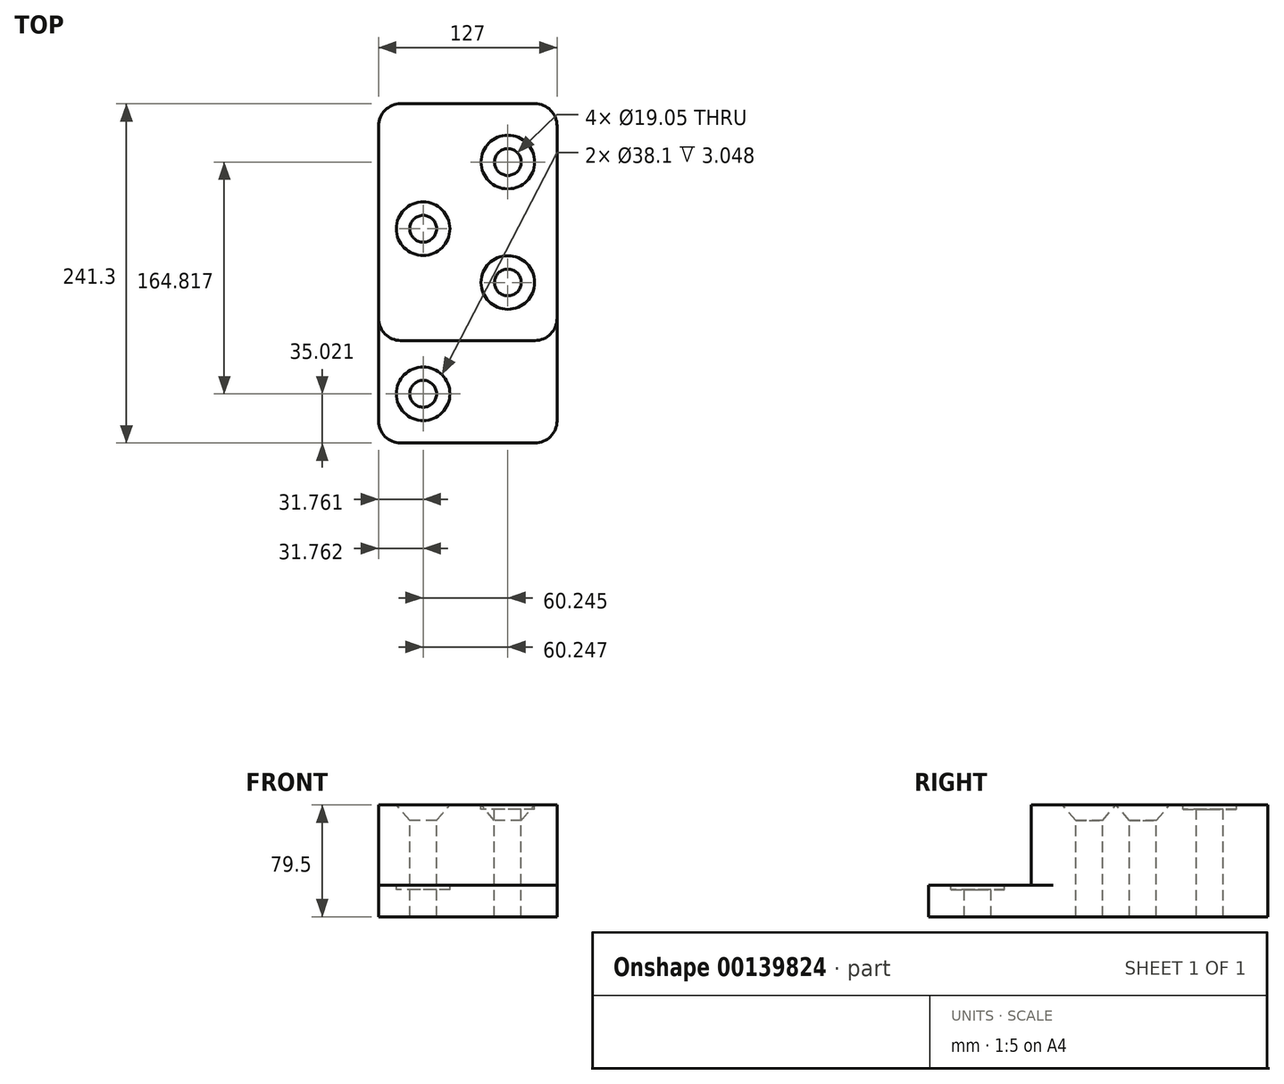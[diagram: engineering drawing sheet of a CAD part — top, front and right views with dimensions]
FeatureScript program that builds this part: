
annotation { "Feature Type Name" : "Feature", "Feature Type Description" : "" }
export const myFeature = defineFeature(function(context is Context, id is Id, definition is map)
    precondition{}
    {
        {
            var Q0;
            Q0=qCreatedBy(makeId("Top.planeOp"),FACE);
            var sketch = newSketch(context, id + "F0", { "sketchPlane" : qUnion([Q0])});
            skLineSegment(sketch, "E0", {"start": v(-63.5, 0) * mm, "end": v(63.5, 0) * mm});
            skLineSegment(sketch, "E1", {"start": v(-63.5, 0) * mm, "end": v(-63.5, -72.9) * mm});
            skLineSegment(sketch, "E2", {"start": v(-63.5, -72.9) * mm, "end": v(63.5, -72.9) * mm});
            skLineSegment(sketch, "E3", {"start": v(63.5, -72.9) * mm, "end": v(63.5, 0) * mm});
            skLineSegment(sketch, "E4", {"start": v(-63.5, 0) * mm, "end": v(-63.5, 168.4) * mm});
            skLineSegment(sketch, "E5", {"start": v(-63.5, 168.4) * mm, "end": v(63.5, 168.4) * mm});
            skLineSegment(sketch, "E6", {"start": v(63.5, 168.4) * mm, "end": v(63.5, 0) * mm});
            skSolve(sketch);
        }
        {
            var Q0;
            Q0=makeQuery(id+"F0.imprint","IMPRINT",FACE,{"disambiguationData":[TD([[makeQuery(id+"F0.imprint","IMPRINT",EDGE,{"derivedFrom":sQuery(id+"F0.wireOp",EDGE,"E0")}),1.0]])]});
            extrude(context, id + "F1", {"entities" : qUnion([Q0]), "depth" : 79.5 * mm});
        }
        {
            var Q0;
            Q0=makeQuery(id+"F0.imprint","IMPRINT",FACE,{"disambiguationData":[TD([[makeQuery(id+"F0.imprint","IMPRINT",EDGE,{"derivedFrom":sQuery(id+"F0.wireOp",EDGE,"E0")}),-1.0]])]});
            extrude(context, id + "F2", {"entities" : qUnion([Q0]), "operationType" : NewBodyOperationType.ADD, "depth" : 22.35 * mm});
        }
        {
            var Q0;
            Q0=makeQuery(id+"F1.opExtrude","CAP_FACE",FACE,{"disambiguationData":[OSD([sQuery(id+"F0.wireOp",EDGE,"E0"),sQuery(id+"F0.wireOp",EDGE,"E4"),sQuery(id+"F0.wireOp",EDGE,"E5"),sQuery(id+"F0.wireOp",EDGE,"E6")])],"isStart":false});
            var sketch = newSketch(context, id + "F3", { "sketchPlane" : qUnion([Q0])});
            skPoint(sketch, "E7", {"position": v(28.5, 126.94) * mm});
            skPoint(sketch, "E8", {"position": v(-31.74, 79.5) * mm});
            skPoint(sketch, "E9", {"position": v(28.48, 41.29) * mm});
            skPoint(sketch, "E10", {"position": v(-31.74, -37.88) * mm});
            skSolve(sketch);
        }
        {
            var Q0;
            Q0=sQuery(id+"F3.wireOp",VERTEX,"E7");
            var Q1;
            Q1=sQuery(id+"F3.wireOp",VERTEX,"E10");
            var Q2;
            Q2=makeQuery(id+"F1.opExtrude","SWEPT_BODY",BODY,{"disambiguationData":[OSD([sQuery(id+"F0.wireOp",EDGE,"E0"),sQuery(id+"F0.wireOp",EDGE,"E4"),sQuery(id+"F0.wireOp",EDGE,"E5"),sQuery(id+"F0.wireOp",EDGE,"E6")])]});
            hole(context, id + "F4", {"style" : HoleStyle.C_BORE, "endStyle" : HoleEndStyle.THROUGH, "holeDiameter" : 19.05 * mm, "cBoreDiameter" : 38.1 * mm, "cBoreDepth" : 3.05 * mm, "locations" : qUnion([Q0, Q1]), "scope" : qUnion([Q2]), "isTappedThrough" : true});
        }
        {
            var Q0;
            Q0=sQuery(id+"F3.wireOp",VERTEX,"E8");
            var Q1;
            Q1=sQuery(id+"F3.wireOp",VERTEX,"E9");
            var Q2;
            Q2=makeQuery(id+"F1.opExtrude","SWEPT_BODY",BODY,{"disambiguationData":[OSD([sQuery(id+"F0.wireOp",EDGE,"E0"),sQuery(id+"F0.wireOp",EDGE,"E4"),sQuery(id+"F0.wireOp",EDGE,"E5"),sQuery(id+"F0.wireOp",EDGE,"E6")])]});
            hole(context, id + "F5", {"style" : HoleStyle.C_SINK, "endStyle" : HoleEndStyle.THROUGH, "holeDiameter" : 19.05 * mm, "cSinkDiameter" : 38.1 * mm, "cSinkAngle" : 82 * degree, "locations" : qUnion([Q0, Q1]), "scope" : qUnion([Q2]), "isTappedThrough" : true});
        }
        {
            var Q0;
            Q0=makeQuery(id+"F1.opExtrude","SWEPT_EDGE",EDGE,{"disambiguationData":[OSD([sQuery(id+"F0.wireOp",EDGE,"E0"),sQuery(id+"F0.wireOp",EDGE,"E3"),sQuery(id+"F0.wireOp",EDGE,"E6")])]});
            var Q1;
            Q1=makeQuery(id+"F1.opExtrude","SWEPT_EDGE",EDGE,{"disambiguationData":[OSD([sQuery(id+"F0.wireOp",EDGE,"E0"),sQuery(id+"F0.wireOp",EDGE,"E1"),sQuery(id+"F0.wireOp",EDGE,"E4")])]});
            var Q2;
            Q2=makeQuery(id+"F2.opExtrude","SWEPT_EDGE",EDGE,{"disambiguationData":[OSD([sQuery(id+"F0.wireOp",EDGE,"E2"),sQuery(id+"F0.wireOp",EDGE,"E3")])]});
            var Q3;
            Q3=makeQuery(id+"F2.opExtrude","SWEPT_EDGE",EDGE,{"disambiguationData":[OSD([sQuery(id+"F0.wireOp",EDGE,"E1"),sQuery(id+"F0.wireOp",EDGE,"E2")])]});
            var Q4;
            Q4=makeQuery(id+"F1.opExtrude","SWEPT_EDGE",EDGE,{"disambiguationData":[OSD([sQuery(id+"F0.wireOp",EDGE,"E5"),sQuery(id+"F0.wireOp",EDGE,"E6")])]});
            var Q5;
            Q5=makeQuery(id+"F1.opExtrude","SWEPT_EDGE",EDGE,{"disambiguationData":[OSD([sQuery(id+"F0.wireOp",EDGE,"E4"),sQuery(id+"F0.wireOp",EDGE,"E5")])]});
            fillet(context, id + "F6", {"entities" : qUnion([Q0, Q1, Q2, Q3, Q4, Q5]), "radius" : 15.75 * mm, "tangentPropagation" : true, "allowEdgeOverflow" : false});
        }
    });
